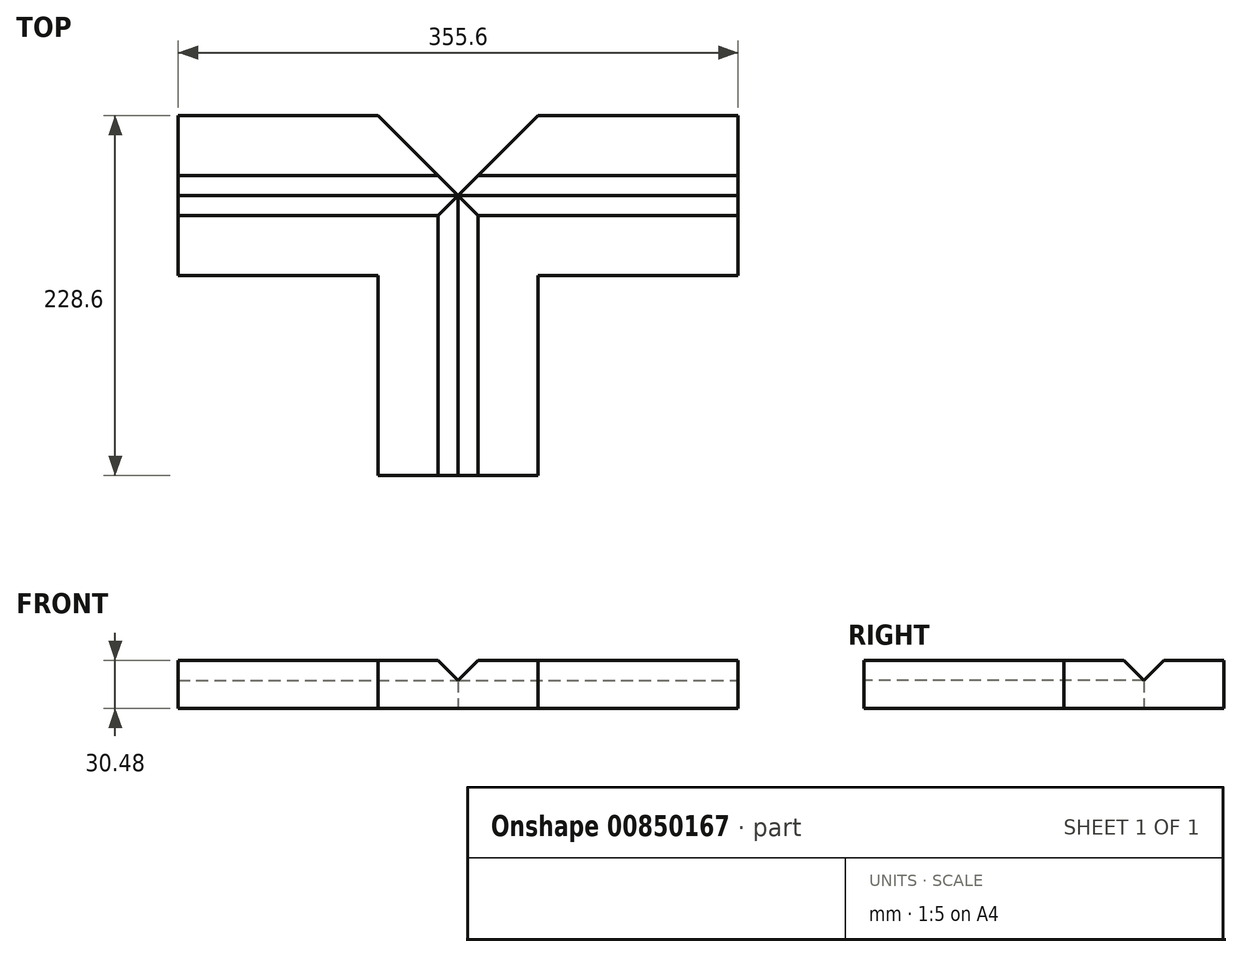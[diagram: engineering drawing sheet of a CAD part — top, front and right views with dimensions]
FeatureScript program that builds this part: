
annotation { "Feature Type Name" : "Feature", "Feature Type Description" : "" }
export const myFeature = defineFeature(function(context is Context, id is Id, definition is map)
    precondition{}
    {
        {
            var Q0;
            Q0=qCreatedBy(makeId("Top.planeOp"),FACE);
            var sketch = newSketch(context, id + "F0", { "sketchPlane" : qUnion([Q0])});
            skLineSegment(sketch, "E0", {"start": v(289.72, -110.56) * mm, "end": v(289.72, 67.24) * mm});
            skLineSegment(sketch, "E1", {"start": v(289.72, 67.24) * mm, "end": v(238.92, 118.04) * mm});
            skLineSegment(sketch, "E2", {"start": v(238.92, 118.04) * mm, "end": v(111.92, 118.04) * mm});
            skLineSegment(sketch, "E3", {"start": v(111.92, 118.04) * mm, "end": v(111.92, 16.44) * mm});
            skLineSegment(sketch, "E4", {"start": v(111.92, 16.44) * mm, "end": v(238.92, 16.44) * mm});
            skLineSegment(sketch, "E5", {"start": v(238.92, 16.44) * mm, "end": v(238.92, -110.56) * mm});
            skLineSegment(sketch, "E6", {"start": v(238.92, -110.56) * mm, "end": v(289.72, -110.56) * mm});
            skLineSegment(sketch, "E7", {"start": v(289.72, 67.24) * mm, "end": v(111.92, 67.24) * mm});
            skPoint(sketch, "E7.endSnap0", {"position": v(111.92, 67.24) * mm});
            skLineSegment(sketch, "E8.MirrorCS", {"start": v(289.72, 67.24) * mm, "end": v(340.52, 118.04) * mm});
            skLineSegment(sketch, "E9.MirrorCS", {"start": v(289.72, 67.24) * mm, "end": v(467.52, 67.24) * mm});
            skLineSegment(sketch, "E10.MirrorCS", {"start": v(467.52, 118.04) * mm, "end": v(467.52, 16.44) * mm});
            skLineSegment(sketch, "E11.MirrorCS", {"start": v(467.52, 16.44) * mm, "end": v(340.52, 16.44) * mm});
            skLineSegment(sketch, "E12.MirrorCS", {"start": v(340.52, 118.04) * mm, "end": v(467.52, 118.04) * mm});
            skLineSegment(sketch, "E13.MirrorCS", {"start": v(340.52, 16.44) * mm, "end": v(340.52, -110.56) * mm});
            skLineSegment(sketch, "E14.MirrorCS", {"start": v(340.52, -110.56) * mm, "end": v(289.72, -110.56) * mm});
            skSolve(sketch);
        }
        {
            var Q0;
            Q0 = qSketchRegion(id + "F0", true);
            extrude(context, id + "F1", {"entities" : qUnion([Q0]), "depth" : 30.48 * mm, "offsetDistance" : 25.4 * mm});
        }
        {
            var Q0;
            Q0=makeQuery(id+"F1.opExtrude","SWEPT_FACE",FACE,{"disambiguationData":[OSD([sQuery(id+"F0.wireOp",EDGE,"E6"),sQuery(id+"F0.wireOp",EDGE,"E14.MirrorCS")])]});
            var sketch = newSketch(context, id + "F2", { "sketchPlane" : qUnion([Q0])});
            skPoint(sketch, "E15.0", {"position": v(289.72, 30.48) * mm});
            skLineSegment(sketch, "E16.0", {"start": v(238.92, 30.48) * mm, "end": v(340.52, 30.48) * mm});
            skLineSegment(sketch, "E17", {"start": v(277.02, 30.48) * mm, "end": v(289.72, 17.78) * mm});
            skLineSegment(sketch, "E18", {"start": v(289.72, 17.78) * mm, "end": v(302.42, 30.48) * mm});
            skSolve(sketch);
        }
        {
            var Q0;
            Q0 = qSketchRegion(id + "F2", true);
            extrude(context, id + "F3", {"entities" : qUnion([Q0]), "operationType" : NewBodyOperationType.REMOVE, "endBound" : BoundingType.THROUGH_ALL, "oppositeDirection" : true, "depth" : 25.4 * mm, "offsetDistance" : 25.4 * mm});
        }
        {
            var Q0;
            Q0=makeQuery(id+"F1.opExtrude","SWEPT_FACE",FACE,{"disambiguationData":[OSD([sQuery(id+"F0.wireOp",EDGE,"E10.MirrorCS")])]});
            var sketch = newSketch(context, id + "F4", { "sketchPlane" : qUnion([Q0])});
            skLineSegment(sketch, "E19.0", {"start": v(118.04, 30.48) * mm, "end": v(16.44, 30.48) * mm});
            skLineSegment(sketch, "E20", {"start": v(54.54, 30.48) * mm, "end": v(67.24, 17.78) * mm});
            skPoint(sketch, "E20.endSnap0", {"position": v(67.24, 30.48) * mm});
            skLineSegment(sketch, "E21", {"start": v(67.24, 17.78) * mm, "end": v(79.94, 30.48) * mm});
            skSolve(sketch);
        }
        {
            var Q0;
            Q0 = qSketchRegion(id + "F4", true);
            extrude(context, id + "F5", {"entities" : qUnion([Q0]), "operationType" : NewBodyOperationType.REMOVE, "endBound" : BoundingType.THROUGH_ALL, "oppositeDirection" : true, "depth" : 25.4 * mm, "offsetDistance" : 25.4 * mm});
        }
    });
